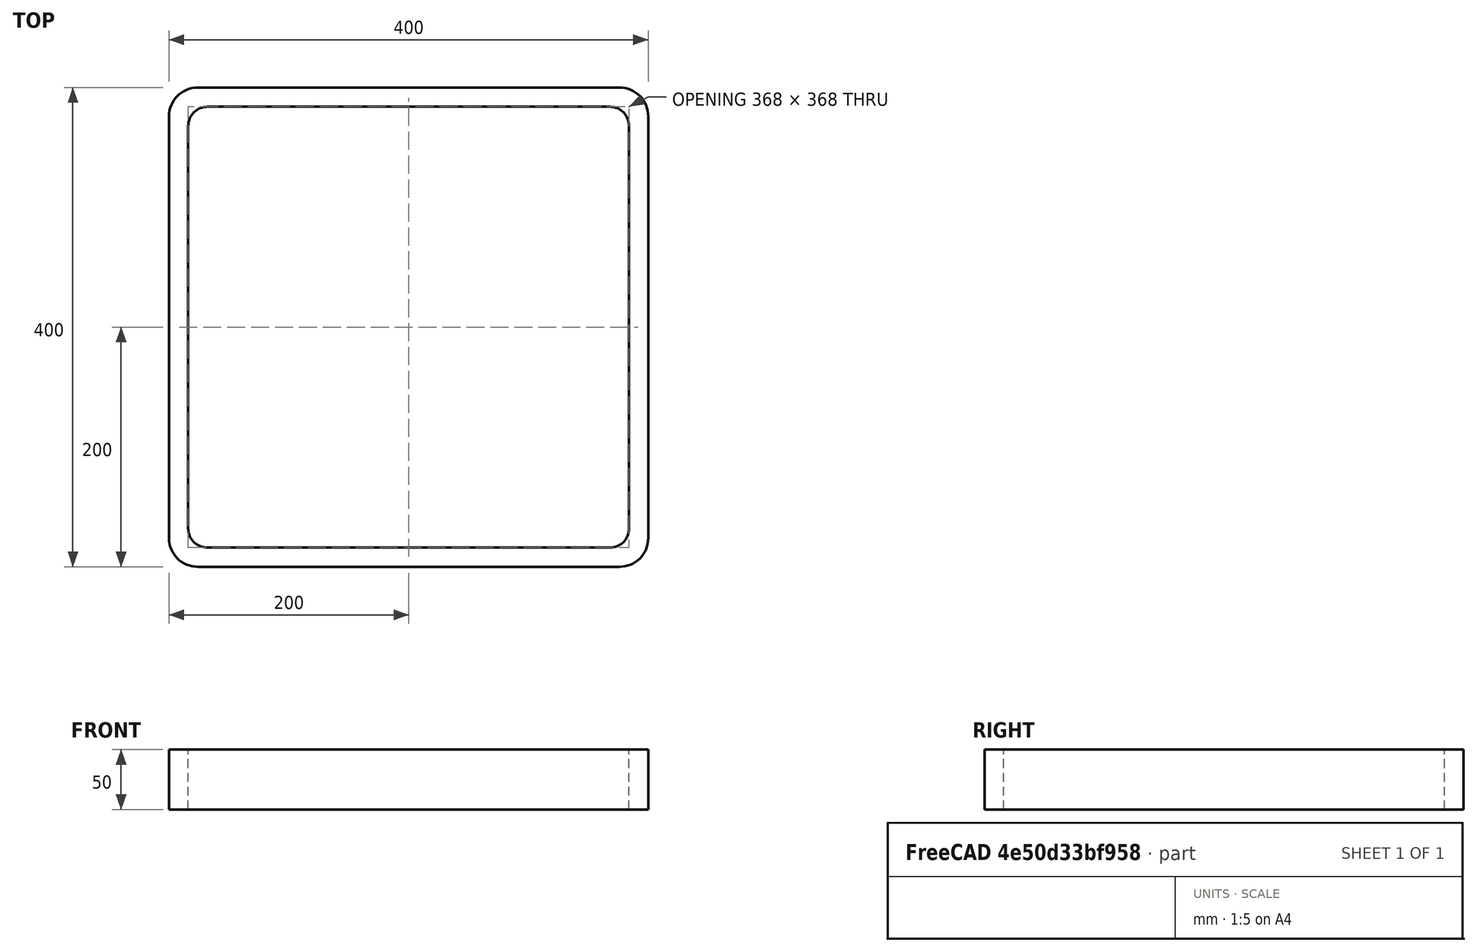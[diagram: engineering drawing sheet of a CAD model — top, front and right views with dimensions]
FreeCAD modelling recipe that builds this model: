
FCSTD DOCUMENT  (FreeCAD 0.15R4671 (Git))
Label: Square hollow section 400x400x16 EN10219 S235JRH
License: All rights reserved
LicenseURL: http://en.wikipedia.org/wiki/All_rights_reserved
objects: Sketcher::SketchObject×1, Part::Extrusion×1
note: 2 computed .brp shape members not serialized (recipe doc carries the construction recipe); baked Part::Feature solids carry a one-line shape summary decoded from their .brp

FEATURE [Sketcher::SketchObject] Sketch
  sketch-geometry (16):
    g0: LineSegment StartX=-168 StartY=184 StartZ=0 EndX=168 EndY=184 EndZ=0
    g1: LineSegment StartX=184 StartY=168 StartZ=0 EndX=184 EndY=-168 EndZ=0
    g2: LineSegment StartX=168 StartY=-184 StartZ=0 EndX=-168 EndY=-184 EndZ=0
    g3: LineSegment StartX=-184 StartY=-168 StartZ=0 EndX=-184 EndY=168 EndZ=0
    g4: LineSegment StartX=-176 StartY=200 StartZ=0 EndX=176 EndY=200 EndZ=0
    g5: LineSegment StartX=200 StartY=176 StartZ=0 EndX=200 EndY=-176 EndZ=0
    g6: LineSegment StartX=176 StartY=-200 StartZ=0 EndX=-176 EndY=-200 EndZ=0
    g7: LineSegment StartX=-200 StartY=-176 StartZ=0 EndX=-200 EndY=176 EndZ=0
    g8: ArcOfCircle CenterX=-168 CenterY=168 CenterZ=0 NormalX=0 NormalY=0 NormalZ=1 Radius=16 StartAngle=1.5708 EndAngle=3.14159
    g9: ArcOfCircle CenterX=168 CenterY=168 CenterZ=0 NormalX=0 NormalY=0 NormalZ=1 Radius=16 StartAngle=0 EndAngle=1.5708
    g10: ArcOfCircle CenterX=168 CenterY=-168 CenterZ=0 NormalX=0 NormalY=0 NormalZ=1 Radius=16 StartAngle=4.71239 EndAngle=6.28319
    g11: ArcOfCircle CenterX=-168 CenterY=-168 CenterZ=0 NormalX=0 NormalY=0 NormalZ=1 Radius=16 StartAngle=3.14159 EndAngle=4.71239
    g12: ArcOfCircle CenterX=176 CenterY=176 CenterZ=0 NormalX=0 NormalY=0 NormalZ=1 Radius=24 StartAngle=0 EndAngle=1.5708
    g13: ArcOfCircle CenterX=176 CenterY=-176 CenterZ=0 NormalX=0 NormalY=0 NormalZ=1 Radius=24 StartAngle=4.71239 EndAngle=6.28319
    g14: ArcOfCircle CenterX=-176 CenterY=-176 CenterZ=0 NormalX=0 NormalY=0 NormalZ=1 Radius=24 StartAngle=3.14159 EndAngle=4.71239
    g15: ArcOfCircle CenterX=-176 CenterY=176 CenterZ=0 NormalX=0 NormalY=0 NormalZ=1 Radius=24 StartAngle=1.5708 EndAngle=3.14159
  constraints (36):
    c: Horizontal(g2)
    c: Vertical(g3)
    c: Horizontal(g6)
    c: Vertical(g7)
    c: Tangent(g3,g8) = 1.5708
    c: Tangent(g0,g8) = 1.5708
    c: Tangent(g0,g9) = 1.5708
    c: Tangent(g1,g9) = 1.5708
    c: Tangent(g1,g10) = 1.5708
    c: Tangent(g2,g10) = 1.5708
    c: Tangent(g2,g11) = 1.5708
    c: Tangent(g3,g11) = 1.5708
    c: Tangent(g4,g12) = 1.5708
    c: Tangent(g5,g12) = 1.5708
    c: Tangent(g5,g13) = 1.5708
    c: Tangent(g6,g13) = 1.5708
    c: Tangent(g6,g14) = 1.5708
    c: Tangent(g7,g14) = 1.5708
    c: Tangent(g7,g15) = 1.5708
    c: Tangent(g4,g15) = 1.5708
    c: Equal(g9,g8)
    c: Equal(g9,g11)
    c: Equal(g9,g10)
    c: Equal(g12,g15)
    c: Equal(g12,g14)
    c: Equal(g12,g13)
    c: Symmetric(g4,g6,g-1)
    c: Symmetric(g7,g5,g-2)
    c: DistanceY(g4,g6) = -400
    c: DistanceX(g7,g5) = 400
    c: Symmetric(g3,g1,g-2)
    c: Symmetric(g0,g2,g-1)
    c: DistanceY(g0,g4) = 16
    c: DistanceX(g5,g1) = -16
    c: Radius(g9) = 16
    c: Radius(g12) = 24
FEATURE [Part::Extrusion] Extrude  label="Square hollow section 400x400x16 EN10219 S235JRH"
  Base = -> Sketch
  Dir = (0,0,50)
  Solid = true
